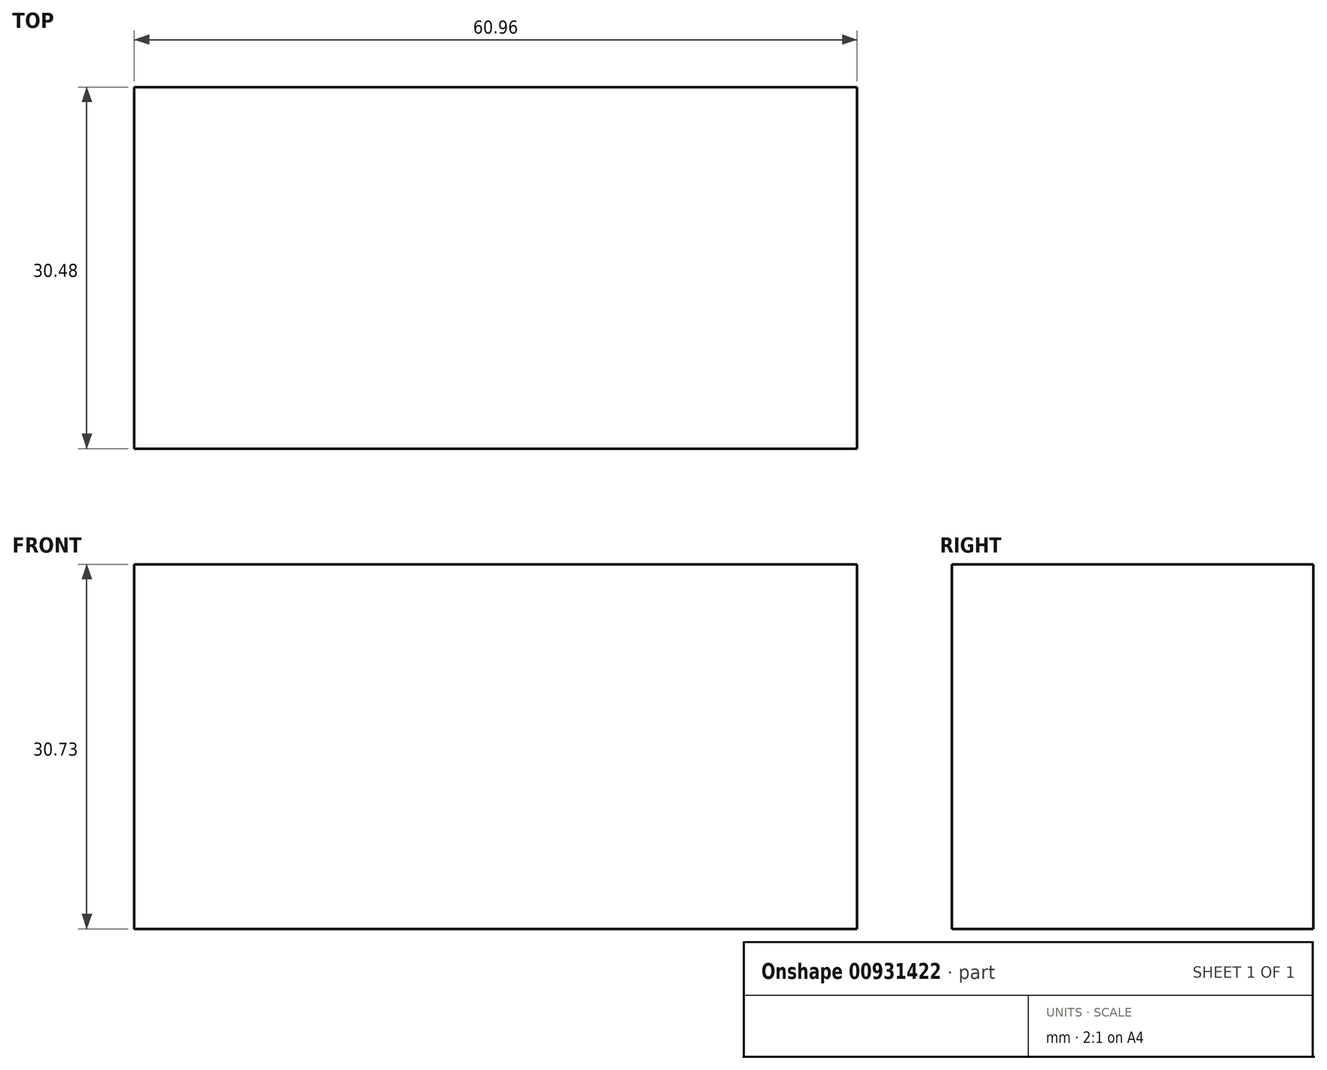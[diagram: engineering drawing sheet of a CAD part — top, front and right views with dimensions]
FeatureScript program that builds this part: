
annotation { "Feature Type Name" : "Feature", "Feature Type Description" : "" }
export const myFeature = defineFeature(function(context is Context, id is Id, definition is map)
    precondition{}
    {
        {
            var Q0;
            Q0=qCreatedBy(makeId("Top.planeOp"),FACE);
            var sketch = newSketch(context, id + "F0", { "sketchPlane" : qUnion([Q0])});
            skLineSegment(sketch, "E0.bottom", {"start": v(0, 0) * mm, "end": v(60.96, 0) * mm});
            skLineSegment(sketch, "E0.top", {"start": v(0, 30.48) * mm, "end": v(60.96, 30.48) * mm});
            skLineSegment(sketch, "E0.left", {"start": v(0, 0) * mm, "end": v(0, 30.48) * mm});
            skLineSegment(sketch, "E0.right", {"start": v(60.96, 0) * mm, "end": v(60.96, 30.48) * mm});
            skSolve(sketch);
        }
        {
            var Q0;
            Q0=makeQuery(id+"F0.imprint","IMPRINT",FACE,{"disambiguationData":[TD([[makeQuery(id+"F0.imprint","IMPRINT",EDGE,{"derivedFrom":sQuery(id+"F0.wireOp",EDGE,"E0.bottom")}),1.0]])]});
            extrude(context, id + "F1", {"entities" : qUnion([Q0]), "depth" : 30.73 * mm, "offsetDistance" : 25.4 * mm});
        }
    });
